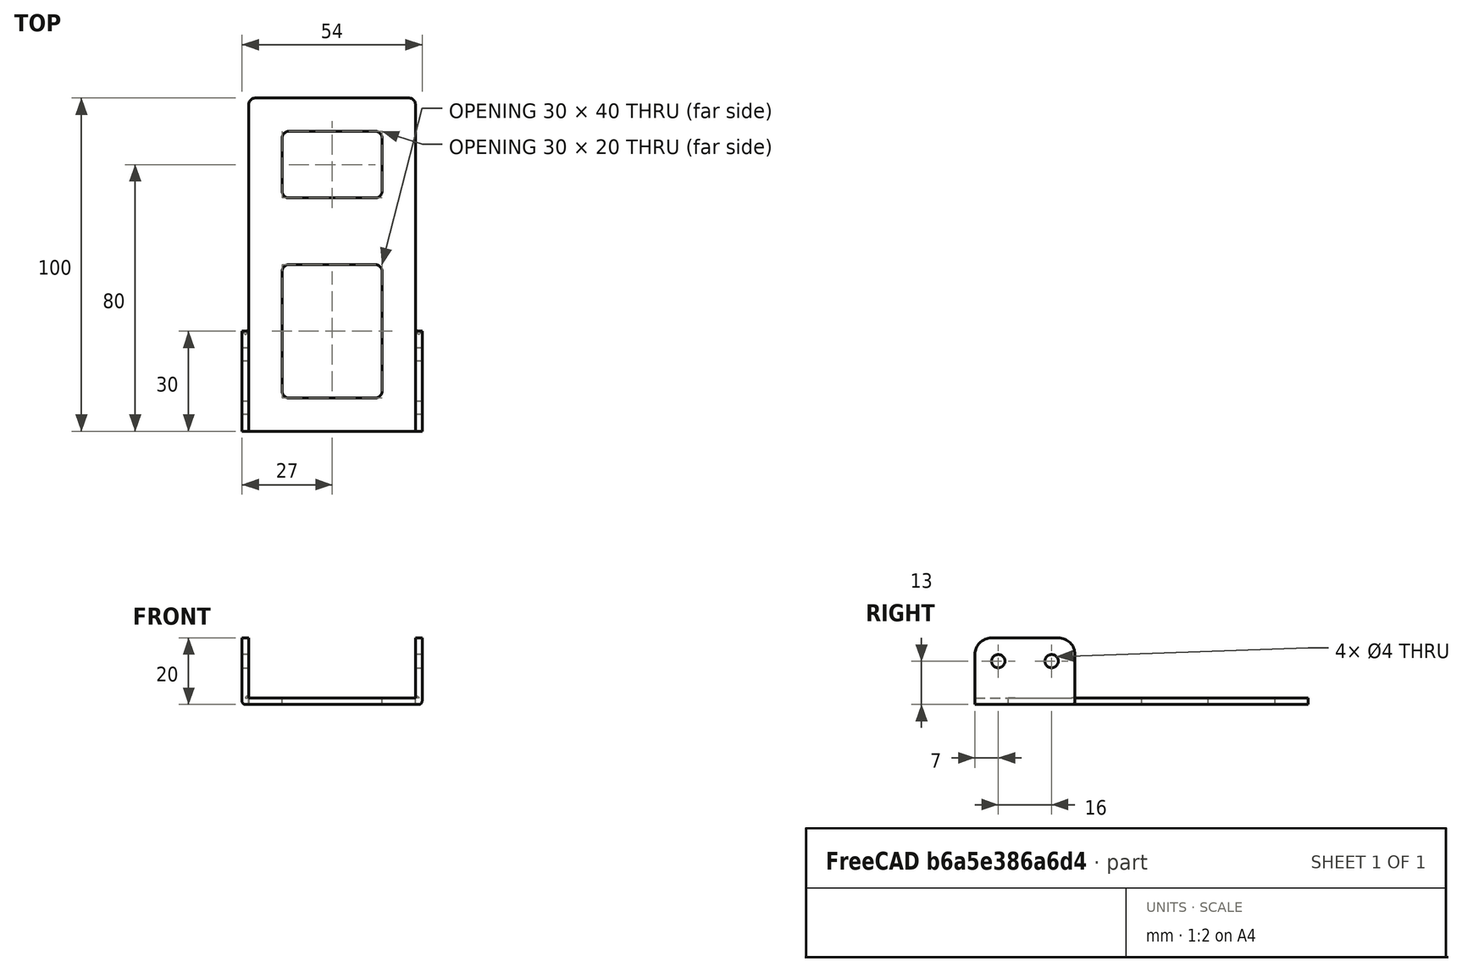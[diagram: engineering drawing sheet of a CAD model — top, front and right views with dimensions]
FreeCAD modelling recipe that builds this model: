
FCSTD DOCUMENT  (FreeCAD 0.21R33694 (Git))
Label: OJT1_T12P03.fumada
License: All rights reserved
LicenseURL: http://en.wikipedia.org/wiki/All_rights_reserved
objects: Part::Fillet×9, Part::Cut×6, Part::Box×5, Part::Cylinder×4, Part::Fuse×2
note: 26 computed .brp shape members not serialized (recipe doc carries the construction recipe); baked Part::Feature solids carry a one-line shape summary decoded from their .brp

FEATURE [Part::Box] Box  label="Cub"
  AttacherType = Attacher::AttachEngine3D
  Height = 2
  Length = 50
  Width = 100
FEATURE [Part::Box] Box001  label="Cub001"
  AttacherType = Attacher::AttachEngine3D
  Height = 10
  Length = 30
  Width = 40
FEATURE [Part::Fillet] Fillet
  Base = -> Box001
  Edges = 4 edges r=2: [Edge1,Edge3,Edge5,Edge7]
  Placement = pos=(10,10,0) rot=(0,0,1;0rad)
FEATURE [Part::Box] Box002  label="Cub002"
  AttacherType = Attacher::AttachEngine3D
  Height = 16
  Length = 30
  Width = 20
FEATURE [Part::Fillet] Fillet001
  Base = -> Box002
  Edges = 4 edges r=2: [Edge1,Edge3,Edge5,Edge7]
  Placement = pos=(10,70,0) rot=(0,0,1;0rad)
FEATURE [Part::Fillet] Fillet002
  Base = -> Box
  Edges = 2 edges r=2: [Edge3,Edge7]
FEATURE [Part::Cut] Cut
  Base = -> Fillet002
  Refine = true
  Tool = -> Fillet
FEATURE [Part::Cut] Cut001
  Base = -> Cut
  Refine = true
  Tool = -> Fillet001
FEATURE [Part::Box] Box003  label="Cub003"
  AttacherType = Attacher::AttachEngine3D
  Height = 20
  Length = 2
  Width = 30
FEATURE [Part::Fillet] Fillet003
  Base = -> Box003
  Edges = 1 edges r=5: [Edge12]
  Placement = pos=(13,0,0) rot=(0,0,1;0rad)
FEATURE [Part::Fillet] Fillet004
  Base = -> Fillet003
  Edges = 1 edges r=5: [Edge6]
  Placement = pos=(-12,0,0) rot=(0,0,1;0rad)
FEATURE [Part::Cylinder] Cylinder  label="Cilindre"
  Angle = 360
  AttacherType = Attacher::AttachEngine3D
  FirstAngle = 0
  Height = 10
  Placement = pos=(-1,7,13) rot=(0,1,0;1.5708rad)
  Radius = 2
  SecondAngle = 0
FEATURE [Part::Cylinder] Cylinder001  label="Cilindre001"
  Angle = 360
  AttacherType = Attacher::AttachEngine3D
  FirstAngle = 0
  Height = 10
  Placement = pos=(-1,23,13) rot=(0,1,0;1.5708rad)
  Radius = 2
  SecondAngle = 0
FEATURE [Part::Cut] Cut002
  Base = -> Fillet004
  Refine = true
  Tool = -> Cylinder
FEATURE [Part::Cut] Cut003
  Base = -> Cut002
  Placement = pos=(-3,0,0) rot=(0,0,1;0rad)
  Refine = true
  Tool = -> Cylinder001
FEATURE [Part::Box] Box004  label="Cub004"
  AttacherType = Attacher::AttachEngine3D
  Height = 20
  Length = 2
  Width = 30
FEATURE [Part::Cylinder] Cylinder002  label="Cilindre002"
  Angle = 360
  AttacherType = Attacher::AttachEngine3D
  FirstAngle = 0
  Height = 10
  Placement = pos=(-1,7,13) rot=(0,1,0;1.5708rad)
  Radius = 2
  SecondAngle = 0
FEATURE [Part::Cylinder] Cylinder003  label="Cilindre003"
  Angle = 360
  AttacherType = Attacher::AttachEngine3D
  FirstAngle = 0
  Height = 10
  Placement = pos=(-1,23,13) rot=(0,1,0;1.5708rad)
  Radius = 2
  SecondAngle = 0
FEATURE [Part::Fillet] Fillet005
  Base = -> Box004
  Edges = 1 edges r=5: [Edge12]
  Placement = pos=(13,0,0) rot=(0,0,1;0rad)
FEATURE [Part::Fillet] Fillet006
  Base = -> Fillet005
  Edges = 1 edges r=5: [Edge6]
  Placement = pos=(-12,0,0) rot=(0,0,1;0rad)
FEATURE [Part::Cut] Cut004
  Base = -> Fillet006
  Refine = true
  Tool = -> Cylinder002
FEATURE [Part::Cut] Cut005
  Base = -> Cut004
  Placement = pos=(49,0,0) rot=(0,0,1;0rad)
  Refine = true
  Tool = -> Cylinder003
FEATURE [Part::Fuse] Fusion
  Base = -> Cut001
  Refine = true
  Tool = -> Cut003
FEATURE [Part::Fuse] Fusion001
  Base = -> Cut005
  Refine = true
  Tool = -> Fusion
FEATURE [Part::Fillet] Fillet007
  Base = -> Fusion001
  Edges = 4 edges r=1: [Edge15,Edge47,Edge102,Edge111]
FEATURE [Part::Fillet] Fillet008
  Base = -> Fillet007
  Edges = 4 edges r=1: [Edge3,Edge13,Edge100,Edge102]
